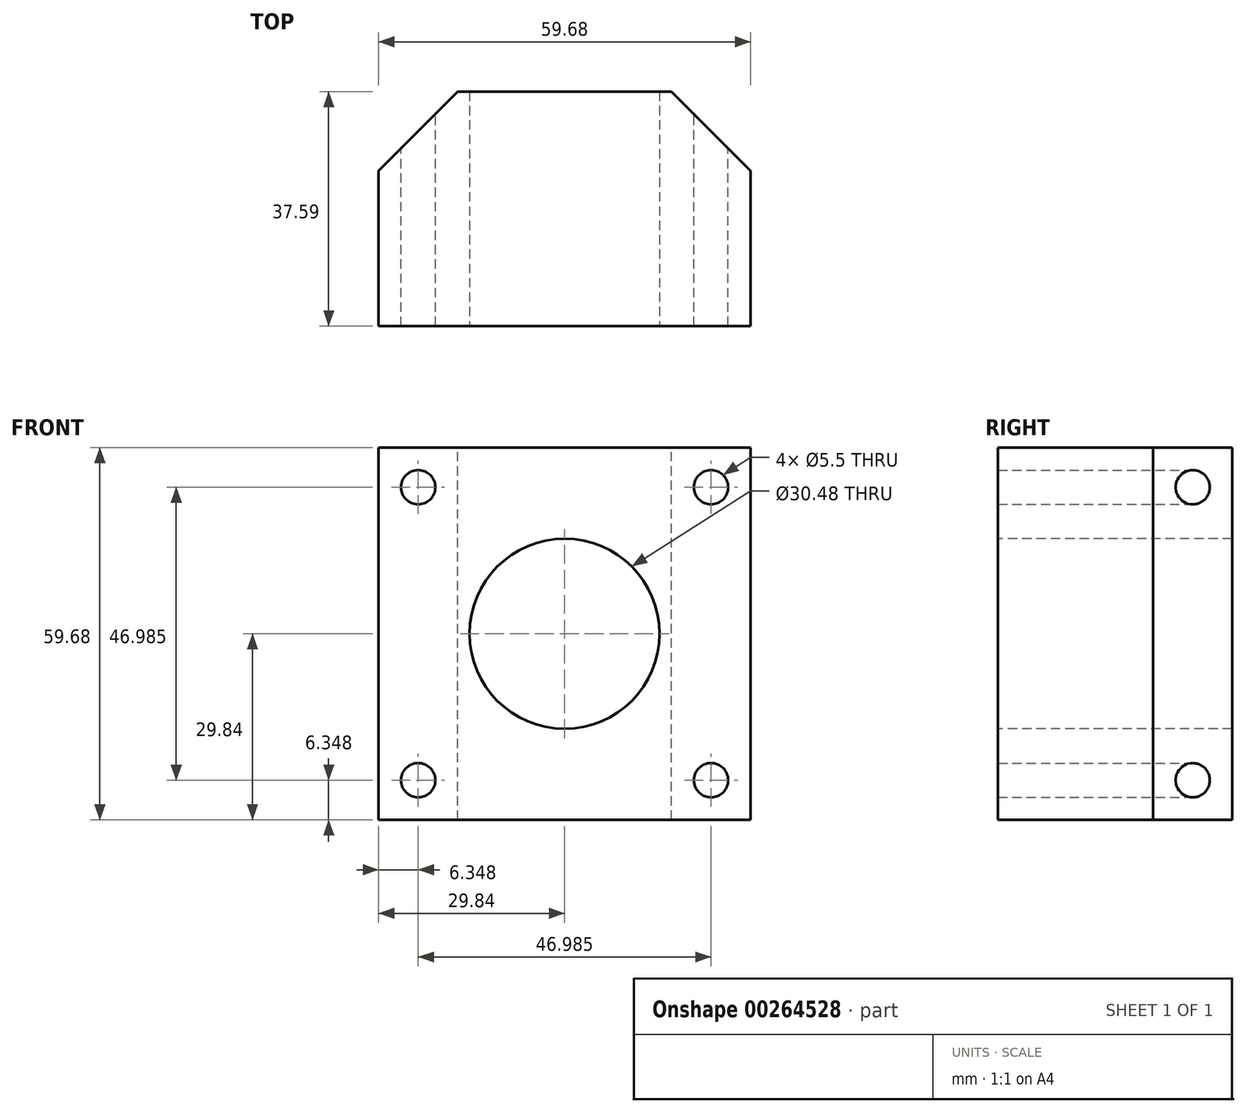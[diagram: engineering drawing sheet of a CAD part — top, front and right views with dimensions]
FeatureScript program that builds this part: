
annotation { "Feature Type Name" : "Feature", "Feature Type Description" : "" }
export const myFeature = defineFeature(function(context is Context, id is Id, definition is map)
    precondition{}
    {
        {
            var Q0;
            Q0=qCreatedBy(makeId("Front.planeOp"),FACE);
            var sketch = newSketch(context, id + "F0", { "sketchPlane" : qUnion([Q0])});
            skLineSegment(sketch, "E0.bottom", {"start": v(29.85, 29.85) * mm, "end": v(-29.85, 29.85) * mm});
            skLineSegment(sketch, "E0.top", {"start": v(29.85, -29.85) * mm, "end": v(-29.85, -29.85) * mm});
            skLineSegment(sketch, "E0.left", {"start": v(29.85, 29.85) * mm, "end": v(29.85, -29.85) * mm});
            skLineSegment(sketch, "E0.right", {"start": v(-29.84, 29.85) * mm, "end": v(-29.85, -29.85) * mm});
            skPoint(sketch, "E0.middle", {"position": v(0, 0) * mm});
            skSolve(sketch);
        }
        {
            var Q0;
            Q0=qSketchRegion(id+"F0",true);
            extrude(context, id + "F1", {"entities" : qUnion([Q0]), "depth" : 31.75 * mm + 4.57 * mm + 1.27 * mm});
        }
        {
            var Q0;
            Q0=makeQuery(id+"F1.opExtrude","CAP_FACE",FACE,{"disambiguationData":[OSD([sQuery(id+"F0.wireOp",EDGE,"E0.bottom"),sQuery(id+"F0.wireOp",EDGE,"E0.top"),sQuery(id+"F0.wireOp",EDGE,"E0.left"),sQuery(id+"F0.wireOp",EDGE,"E0.right")])],"isStart":false});
            var sketch = newSketch(context, id + "F2", { "sketchPlane" : qUnion([Q0])});
            skCircle(sketch, "E1", {"center": v(0, 0) * mm, "radius": 15.24 * mm});
            skSolve(sketch);
        }
        {
            var Q0;
            Q0=qSketchRegion(id+"F2",true);
            extrude(context, id + "F3", {"entities" : qUnion([Q0]), "operationType" : NewBodyOperationType.REMOVE, "endBound" : BoundingType.THROUGH_ALL, "oppositeDirection" : true, "depth" : 25.4 * mm});
        }
        {
            var Q0;
            Q0=makeQuery(id+"F1.opExtrude","SWEPT_FACE",FACE,{"disambiguationData":[OSD([sQuery(id+"F0.wireOp",EDGE,"E0.bottom")])]});
            var sketch = newSketch(context, id + "F4", { "sketchPlane" : qUnion([Q0])});
            skLineSegment(sketch, "E2", {"start": v(-17.14, 0) * mm, "end": v(-29.85, -12.7) * mm});
            skLineSegment(sketch, "E3", {"start": v(-29.85, -12.7) * mm, "end": v(-29.85, 0) * mm});
            skLineSegment(sketch, "E4", {"start": v(-29.85, 0) * mm, "end": v(-17.14, 0) * mm});
            skLineSegment(sketch, "E5", {"start": v(0, 0) * mm, "end": v(0, -24.44) * mm, "construction": true});
            skLineSegment(sketch, "E6.MirrorCS", {"start": v(29.85, 0) * mm, "end": v(17.14, 0) * mm});
            skLineSegment(sketch, "E7.MirrorCS", {"start": v(29.85, -12.7) * mm, "end": v(29.85, 0) * mm});
            skLineSegment(sketch, "E8.MirrorCS", {"start": v(17.14, 0) * mm, "end": v(29.85, -12.7) * mm});
            skSolve(sketch);
        }
        {
            var Q0;
            Q0 = qSketchRegion(id + "F4", true);
            extrude(context, id + "F5", {"entities" : qUnion([Q0]), "operationType" : NewBodyOperationType.REMOVE, "endBound" : BoundingType.THROUGH_ALL, "oppositeDirection" : true, "depth" : 25.4 * mm});
        }
        {
            var Q0;
            Q0=makeQuery(id+"F1.opExtrude","CAP_FACE",FACE,{"disambiguationData":[OSD([sQuery(id+"F0.wireOp",EDGE,"E0.bottom"),sQuery(id+"F0.wireOp",EDGE,"E0.top"),sQuery(id+"F0.wireOp",EDGE,"E0.left"),sQuery(id+"F0.wireOp",EDGE,"E0.right")])],"isStart":false});
            var sketch = newSketch(context, id + "F6", { "sketchPlane" : qUnion([Q0])});
            skLineSegment(sketch, "E9.bottom", {"start": v(-23.5, 23.5) * mm, "end": v(23.5, 23.5) * mm, "construction": true});
            skLineSegment(sketch, "E9.top", {"start": v(-23.5, -23.5) * mm, "end": v(23.5, -23.5) * mm, "construction": true});
            skLineSegment(sketch, "E9.left", {"start": v(-23.5, 23.5) * mm, "end": v(-23.5, -23.5) * mm, "construction": true});
            skLineSegment(sketch, "E9.right", {"start": v(23.5, 23.5) * mm, "end": v(23.5, -23.5) * mm, "construction": true});
            skPoint(sketch, "E9.middle", {"position": v(0, 0) * mm});
            skSolve(sketch);
        }
        {
            var Q0;
            Q0=sQuery(id+"F6.wireOp",VERTEX,"E9.left.start");
            var Q1;
            Q1=sQuery(id+"F6.wireOp",VERTEX,"E9.right.start");
            var Q2;
            Q2=sQuery(id+"F6.wireOp",VERTEX,"E9.right.end");
            var Q3;
            Q3=sQuery(id+"F6.wireOp",VERTEX,"E9.left.end");
            var Q4;
            Q4=makeQuery(id+"F1.opExtrude","SWEPT_BODY",BODY,{"disambiguationData":[OSD([sQuery(id+"F0.wireOp",EDGE,"E0.bottom"),sQuery(id+"F0.wireOp",EDGE,"E0.top"),sQuery(id+"F0.wireOp",EDGE,"E0.left"),sQuery(id+"F0.wireOp",EDGE,"E0.right")])]});
            hole(context, id + "F7", {"style" : HoleStyle.SIMPLE, "endStyle" : HoleEndStyle.THROUGH, "standardTappedOrClearance" : lookupTablePath({ "standard" : "ISO", "fit" : "Normal", "size" : "M5", "type" : "Clearance" }), "standardBlindInLast" : lookupTablePath({ "fit" : "Standard", "standard" : "ISO", "size" : "M5", "type" : "Clearance" }), "holeDiameter" : 5.5 * mm, "isTappedThrough" : true, "tappedDepth" : 12.7 * mm, "tapClearance" : 3, "locations" : qUnion([Q0, Q1, Q2, Q3]), "scope" : qUnion([Q4]), "startStyle" : HoleStartStyle.PART});
        }
    });
